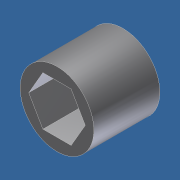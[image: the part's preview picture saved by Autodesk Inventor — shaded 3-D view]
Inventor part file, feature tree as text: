
AUTODESK INVENTOR PART (.ipt)
format: ipt  version: unknown  size: 183,296 bytes
history: native  units: in
note: dims shown in document units (in); Inventor stores cm internally (conversion verified against a paired STEP export)
features: other x1, imported_body x1, extrude x1, sketch x1
ambient origin geometry x8: Origin, YZ Plane, XZ Plane, XY Plane, X Axis, Y Axis, Z Axis, Center Point
feature tree (4):
  other  "Boss-Extrude1"
  imported_body  "Base1"
  extrude  "Extrusion1"  [1 undecoded]
  sketch  "Sketch1"  dims[d0=0.625in d1=0.0in]
note: 1 required parameter value undecoded (feature->parameter linkage not recoverable at this tier; creation-order binding heuristic only, values carry confidence <= 0.55)
